# Revit family: SYSCOOL FLOOR 48 HP R, наружный  блок
name_source: partatom
category: Оборудование
units: mm (PartAtom-declared; Revit-internal decimal feet)

## family parameters
Всегда вертикально = Да
Заголовок OmniClass = Climate Control (HVAC)
На основе рабочей плоскости = Нет
Номер OmniClass = 23.75.00.00
Общий = Нет
При загрузке вырезать с полостями = Нет
Размер круглого соединителя = Использовать радиус
Тип детали = Нормальный
Точка расчета площади = Нет

## types (1)
- MOU-48HN1-R
    Air Flow = 7500.00 м³/ч
    Casing color = SB2098
    Compressor = 1
    Depth = 410 мм
    Gas = R410A
    Gas pipe = 15.9 мм
    Gas pipe Radius = 7.95 мм
    Height = 810 мм
    Installation = Outdoor installation
    Liquid pipe = 9.52 мм
    Liquid pipe Radius = 4.76 мм
    Maximum Fuse Amps = 25 А
    Min cable selection (power wiring) = 5x2.5
    Minimum Circuit Amps = 11 А
    Net Weight = 98.60 кг
    Power supply = 380-415V,3Ph,50Hz
    Width = 946 мм
    clearance access behind = 300 мм
    clearance access front = 2000 мм
    clearance access left = 300 мм
    clearance access right = 600 мм
    Группа модели = MOU-48HN1-R

## geometry (parser evidence)
native form markers: Blend x1, Sweep x19
no freeform markers — native parametric forms only
